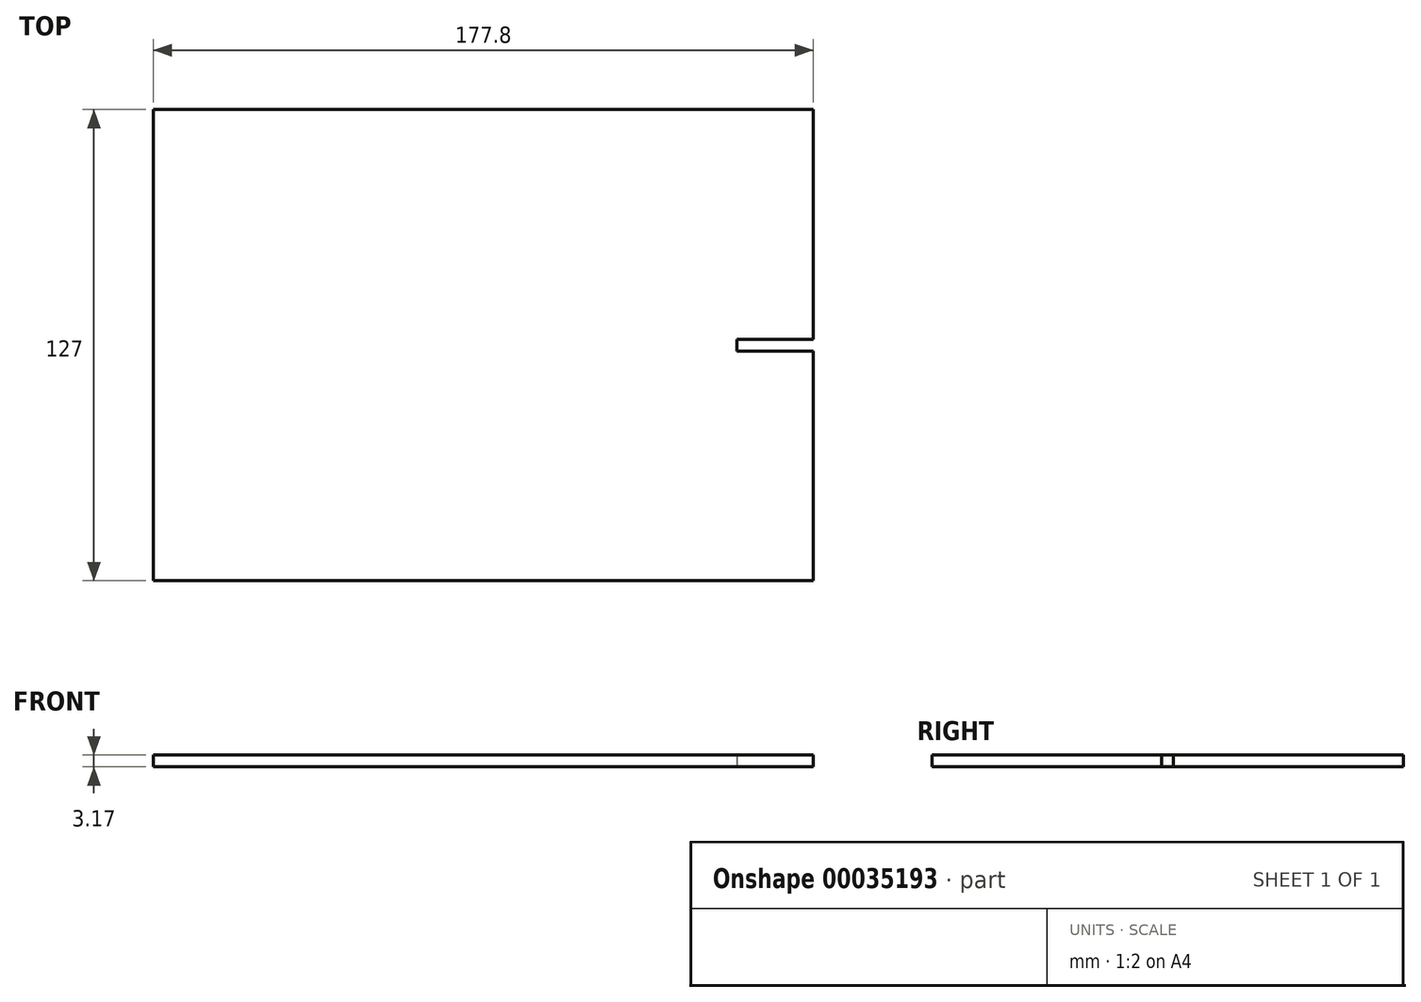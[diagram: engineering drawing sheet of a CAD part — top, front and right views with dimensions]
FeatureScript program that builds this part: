
annotation { "Feature Type Name" : "Feature", "Feature Type Description" : "" }
export const myFeature = defineFeature(function(context is Context, id is Id, definition is map)
    precondition{}
    {
        {
            var Q0;
            Q0=qCreatedBy(makeId("Top.planeOp"),FACE);
            var sketch = newSketch(context, id + "F0", { "sketchPlane" : qUnion([Q0])});
            skLineSegment(sketch, "E0.rect.bottom", {"start": v(88.9, -63.5) * mm, "end": v(-88.9, -63.5) * mm});
            skLineSegment(sketch, "E0.rect.top", {"start": v(88.9, 63.5) * mm, "end": v(-88.9, 63.5) * mm});
            skLineSegment(sketch, "E0.rect.left", {"start": v(88.9, -63.5) * mm, "end": v(88.9, 63.5) * mm});
            skLineSegment(sketch, "E0.rect.right", {"start": v(-88.9, -63.5) * mm, "end": v(-88.9, 63.5) * mm});
            skPoint(sketch, "E0.rect.middle", {"position": v(0, 0) * mm});
            skLineSegment(sketch, "E1", {"start": v(-88.9, 0) * mm, "end": v(88.9, 0) * mm, "construction": true});
            skLineSegment(sketch, "E2", {"start": v(88.9, 1.59) * mm, "end": v(68.26, 1.59) * mm});
            skLineSegment(sketch, "E3", {"start": v(68.26, 1.59) * mm, "end": v(68.26, 0) * mm});
            skLineSegment(sketch, "E4.MirrorCS", {"start": v(88.9, -1.59) * mm, "end": v(68.26, -1.59) * mm});
            skLineSegment(sketch, "E5.MirrorCS", {"start": v(68.26, -1.59) * mm, "end": v(68.26, 0) * mm});
            skSolve(sketch);
        }
        {
            var Q0;
            Q0=makeQuery(id+"F0.imprint","IMPRINT",FACE,{"disambiguationData":[TD([[makeQuery(id+"F0.imprint","IMPRINT",EDGE,{"derivedFrom":sQuery(id+"F0.wireOp",EDGE,"E0.rect.bottom")}),-1.0]])]});
            extrude(context, id + "F1", {"entities" : qUnion([Q0]), "depth" : 3.17 * mm});
        }
    });
